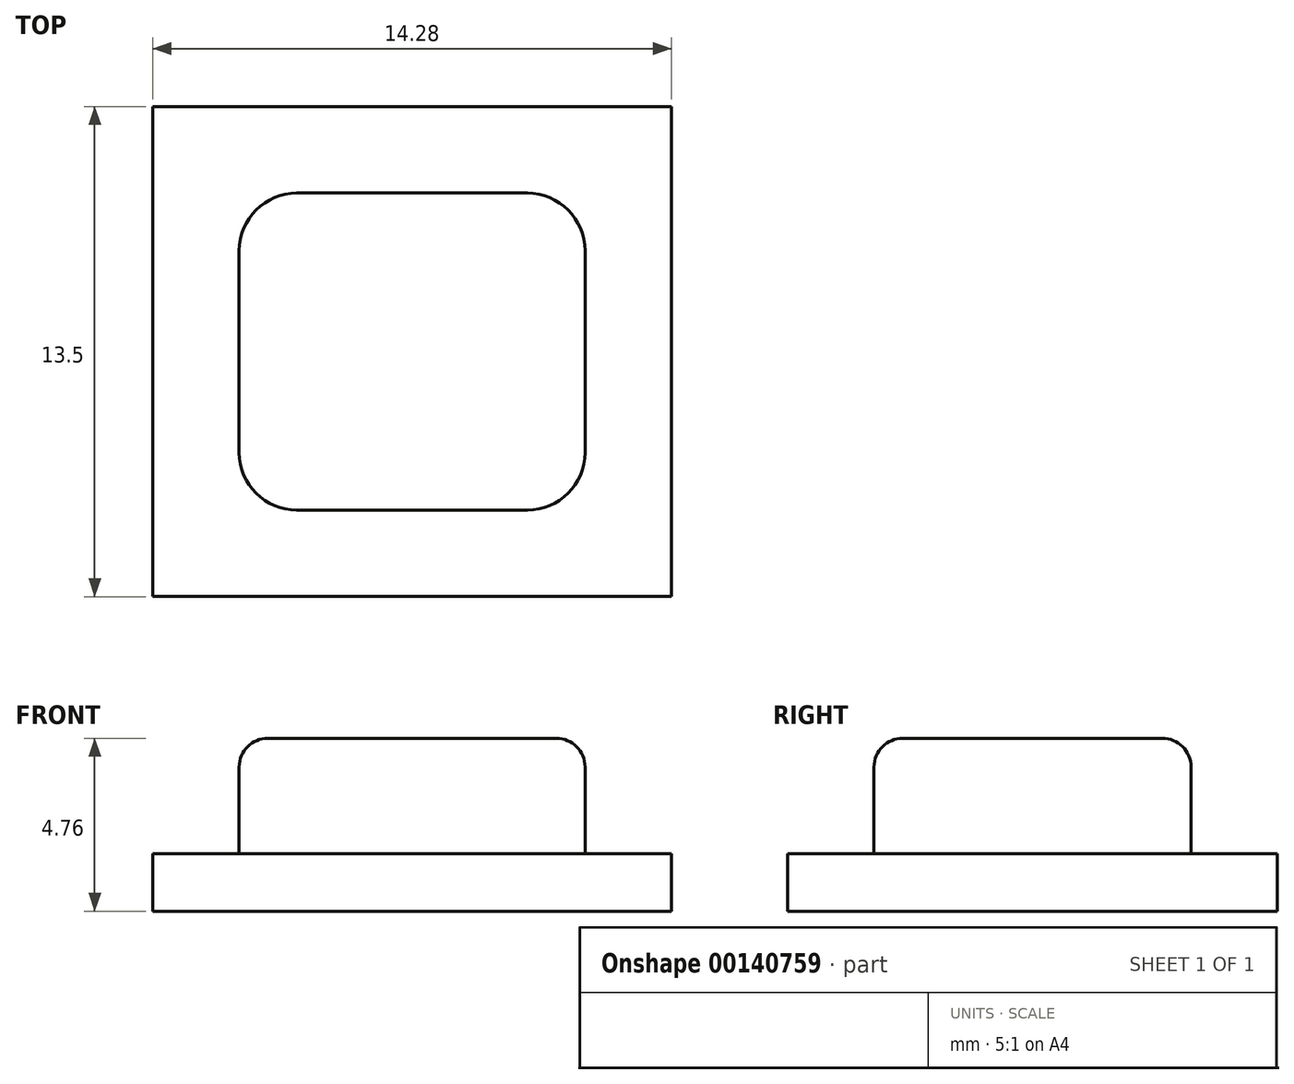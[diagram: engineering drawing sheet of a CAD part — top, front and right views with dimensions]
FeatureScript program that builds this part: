
annotation { "Feature Type Name" : "Feature", "Feature Type Description" : "" }
export const myFeature = defineFeature(function(context is Context, id is Id, definition is map)
    precondition{}
    {
        {
            var Q0;
            Q0=qCreatedBy(makeId("Top.planeOp"),FACE);
            var sketch = newSketch(context, id + "F0", { "sketchPlane" : qUnion([Q0])});
            skLineSegment(sketch, "E0.bottom", {"start": v(7.14, -6.75) * mm, "end": v(-7.14, -6.75) * mm});
            skLineSegment(sketch, "E0.top", {"start": v(7.14, 6.75) * mm, "end": v(-7.14, 6.75) * mm});
            skLineSegment(sketch, "E0.left", {"start": v(7.14, -6.75) * mm, "end": v(7.14, 6.75) * mm});
            skLineSegment(sketch, "E0.right", {"start": v(-7.14, -6.75) * mm, "end": v(-7.14, 6.75) * mm});
            skPoint(sketch, "E0.middle", {"position": v(0, 0) * mm});
            skLineSegment(sketch, "E1.bottom", {"start": v(3.17, -4.37) * mm, "end": v(-3.17, -4.37) * mm});
            skLineSegment(sketch, "E1.top", {"start": v(3.17, 4.37) * mm, "end": v(-3.17, 4.37) * mm});
            skLineSegment(sketch, "E1.left", {"start": v(4.76, -2.78) * mm, "end": v(4.76, 2.78) * mm});
            skLineSegment(sketch, "E1.right", {"start": v(-4.76, -2.78) * mm, "end": v(-4.76, 2.78) * mm});
            skPoint(sketch, "E2.visualSharp", {"position": v(-4.76, 4.37) * mm});
            skArc(sketch, "E2.filletArc", {"start": v(-3.17, 4.37) * mm, "mid": v(-4.3, 3.9) * mm, "end": v(-4.76, 2.78) * mm});
            skPoint(sketch, "E3.visualSharp", {"position": v(4.76, 4.37) * mm});
            skArc(sketch, "E3.filletArc", {"start": v(4.76, 2.78) * mm, "mid": v(4.3, 3.9) * mm, "end": v(3.17, 4.37) * mm});
            skPoint(sketch, "E4.visualSharp", {"position": v(4.76, -4.37) * mm});
            skArc(sketch, "E4.filletArc", {"start": v(3.17, -4.37) * mm, "mid": v(4.3, -3.9) * mm, "end": v(4.76, -2.78) * mm});
            skPoint(sketch, "E5.visualSharp", {"position": v(-4.76, -4.37) * mm});
            skArc(sketch, "E5.filletArc", {"start": v(-4.76, -2.78) * mm, "mid": v(-4.3, -3.9) * mm, "end": v(-3.17, -4.37) * mm});
            skSolve(sketch);
        }
        {
            var Q0;
            Q0 = qSketchRegion(id + "F0", true);
            var Q1;
            Q1=makeQuery(id+"F0.imprint","IMPRINT",FACE,{"disambiguationData":[TD([[makeQuery(id+"F0.imprint","IMPRINT",EDGE,{"derivedFrom":sQuery(id+"F0.wireOp",EDGE,"E1.bottom")}),-1.0]])]});
            extrude(context, id + "F1", {"entities" : qUnion([Q0, Q1]), "depth" : 1.59 * mm});
        }
        {
            var Q0;
            Q0=makeQuery(id+"F1.opExtrude","CAP_FACE",FACE,{"disambiguationData":[OSD([sQuery(id+"F0.wireOp",EDGE,"E0.bottom"),sQuery(id+"F0.wireOp",EDGE,"E0.top"),sQuery(id+"F0.wireOp",EDGE,"E0.left"),sQuery(id+"F0.wireOp",EDGE,"E0.right")])],"isStart":false});
            var sketch = newSketch(context, id + "F2", { "sketchPlane" : qUnion([Q0])});
            skLineSegment(sketch, "E6.0", {"start": v(3.17, 4.37) * mm, "end": v(-3.17, 4.37) * mm});
            skArc(sketch, "E7.0", {"start": v(-3.17, 4.37) * mm, "mid": v(-4.3, 3.9) * mm, "end": v(-4.76, 2.78) * mm});
            skLineSegment(sketch, "E8.0", {"start": v(-4.76, -2.78) * mm, "end": v(-4.76, 2.78) * mm});
            skArc(sketch, "E9.0", {"start": v(-4.76, -2.78) * mm, "mid": v(-4.3, -3.9) * mm, "end": v(-3.17, -4.37) * mm});
            skLineSegment(sketch, "E10.0", {"start": v(3.17, -4.37) * mm, "end": v(-3.17, -4.37) * mm});
            skArc(sketch, "E11.0", {"start": v(3.17, -4.37) * mm, "mid": v(4.3, -3.9) * mm, "end": v(4.76, -2.78) * mm});
            skLineSegment(sketch, "E12.0", {"start": v(4.76, -2.78) * mm, "end": v(4.76, 2.78) * mm});
            skArc(sketch, "E13.0", {"start": v(4.76, 2.78) * mm, "mid": v(4.3, 3.9) * mm, "end": v(3.17, 4.37) * mm});
            skSolve(sketch);
        }
        {
            var Q0;
            Q0=makeQuery(id+"F2.imprint","IMPRINT",FACE,{"disambiguationData":[TD([[makeQuery(id+"F2.imprint","IMPRINT",EDGE,{"derivedFrom":sQuery(id+"F2.wireOp",EDGE,"E6.0")}),1.0]])]});
            extrude(context, id + "F3", {"entities" : qUnion([Q0]), "operationType" : NewBodyOperationType.ADD, "depth" : 3.17 * mm});
        }
        {
            var Q0;
            Q0=makeQuery(id+"F3.opExtrude","CAP_EDGE",EDGE,{"disambiguationData":[OSD([sQuery(id+"F2.wireOp",EDGE,"E12.0")])],"isStart":false});
            fillet(context, id + "F4", {"entities" : qUnion([Q0]), "radius" : 0.8 * mm, "tangentPropagation" : true, "allowEdgeOverflow" : false});
        }
    });
